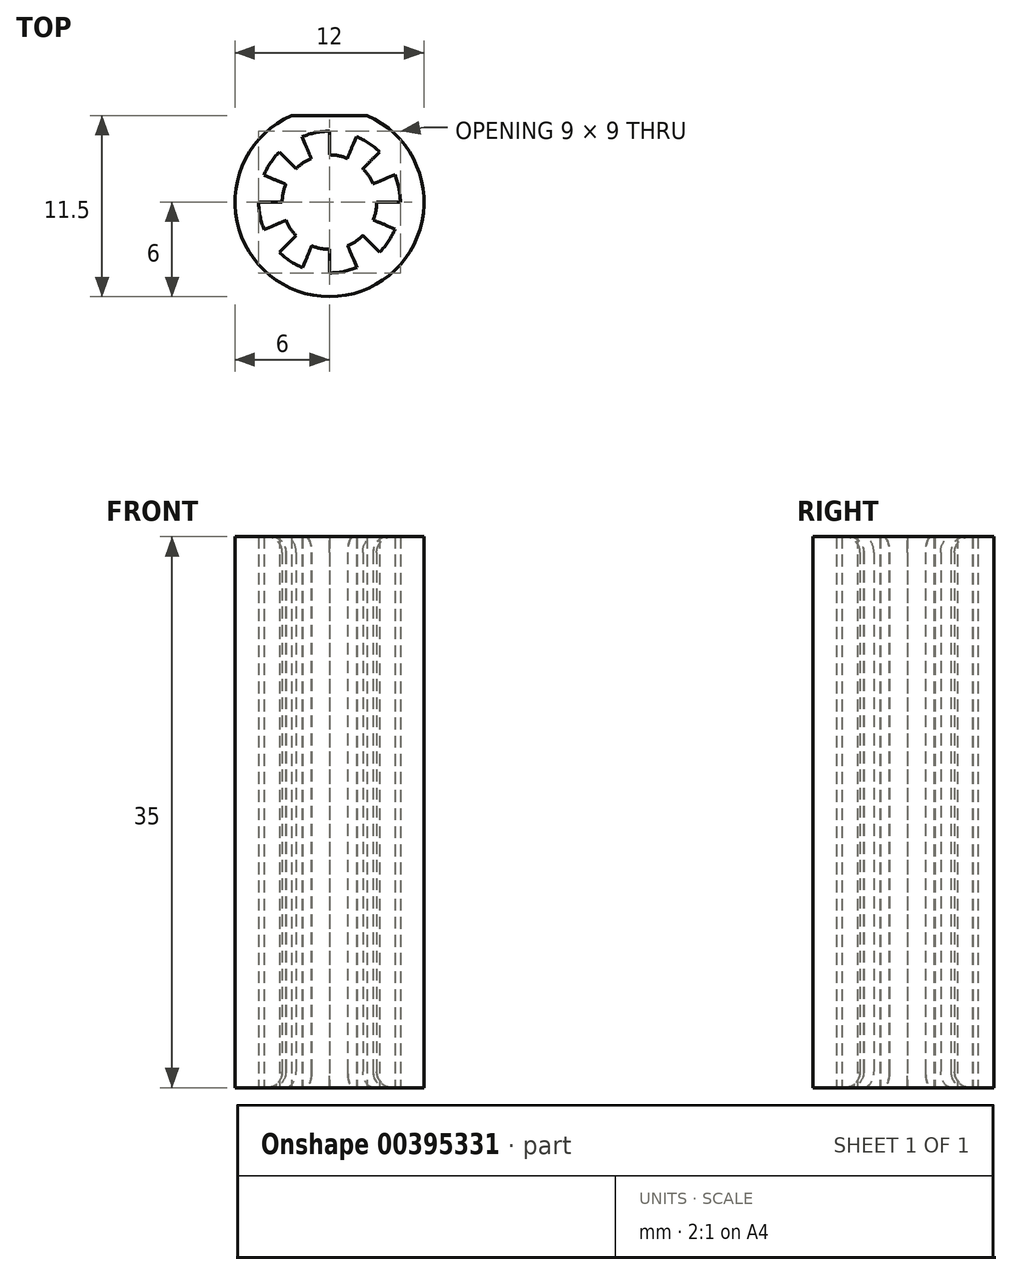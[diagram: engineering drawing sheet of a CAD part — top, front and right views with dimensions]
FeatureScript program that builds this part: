
annotation { "Feature Type Name" : "Feature", "Feature Type Description" : "" }
export const myFeature = defineFeature(function(context is Context, id is Id, definition is map)
    precondition{}
    {
        {
            var Q0;
            Q0=qCreatedBy(makeId("Top.planeOp"),FACE);
            var sketch = newSketch(context, id + "F0", { "sketchPlane" : qUnion([Q0])});
            skCircle(sketch, "E0", {"center": v(0, 0) * mm, "radius": 3 * mm});
            skCircle(sketch, "E1", {"center": v(0, 0) * mm, "radius": 6 * mm});
            skCircle(sketch, "E2", {"center": v(0, 0) * mm, "radius": 4.5 * mm});
            skLineSegment(sketch, "E3", {"start": v(0, 6) * mm, "end": v(0, -6) * mm});
            skLineSegment(sketch, "E4", {"start": v(-6, 0) * mm, "end": v(6, 0) * mm});
            skPoint(sketch, "E5", {"position": v(4.56, 3.9) * mm});
            skPoint(sketch, "E6", {"position": v(-4.24, 4.24) * mm});
            skPoint(sketch, "E7", {"position": v(-4.52, -3.95) * mm});
            skPoint(sketch, "E8", {"position": v(4.86, -3.52) * mm});
            skLineSegment(sketch, "E9", {"start": v(0, 0) * mm, "end": v(-4.24, 4.24) * mm});
            skPoint(sketch, "E10", {"position": v(-2.32, 5.53) * mm});
            skPoint(sketch, "E11", {"position": v(-5.54, 2.3) * mm});
            skLineSegment(sketch, "E12", {"start": v(-5.54, 2.3) * mm, "end": v(0, 0) * mm});
            skLineSegment(sketch, "E13", {"start": v(-2.32, 5.53) * mm, "end": v(0, 0) * mm});
            skSolve(sketch);
        }
        {
            var Q0;
            {var subQ0=sQuery(id+"F0.wireOp",EDGE,"E3");var subQ1=sQuery(id+"F0.wireOp",EDGE,"E1");var subQ2=makeQuery(id+"F0.imprint","INTERSECT",VERTEX,{"disambiguationData":[OD(0.0)],"derivedFrom":[subQ1,subQ0]});Q0=makeQuery(id+"F0.imprint","IMPRINT",FACE,{"disambiguationData":[TD([[makeQuery(id+"F0.imprint","IMPRINT",EDGE,{"disambiguationData":[TD([[subQ2,-1.0]])],"derivedFrom":subQ1}),1.0]])]});}
            var Q1;
            {var subQ0=sQuery(id+"F0.wireOp",EDGE,"E13");var subQ1=sQuery(id+"F0.wireOp",EDGE,"E0");var subQ2=makeQuery(id+"F0.imprint","INTERSECT",VERTEX,{"derivedFrom":[subQ1,subQ0]});Q1=makeQuery(id+"F0.imprint","IMPRINT",FACE,{"disambiguationData":[TD([[makeQuery(id+"F0.imprint","IMPRINT",EDGE,{"disambiguationData":[TD([[subQ2,-1.0]])],"derivedFrom":subQ1}),-1.0]])]});}
            var Q2;
            {var subQ0=sQuery(id+"F0.wireOp",EDGE,"E9");var subQ1=sQuery(id+"F0.wireOp",EDGE,"E1");var subQ2=makeQuery(id+"F0.imprint","INTERSECT",VERTEX,{"derivedFrom":[subQ1,subQ0]});Q2=makeQuery(id+"F0.imprint","IMPRINT",FACE,{"disambiguationData":[TD([[makeQuery(id+"F0.imprint","IMPRINT",EDGE,{"disambiguationData":[TD([[subQ2,1.0]])],"derivedFrom":subQ1}),1.0]])]});}
            extrude(context, id + "F1", {"entities" : qUnion([Q0, Q1, Q2]), "depth" : 35 * mm});
        }
        {
            var Q0;
            Q0=qCreatedBy(makeId("Front.planeOp"),FACE);
            var sketch = newSketch(context, id + "F2", { "sketchPlane" : qUnion([Q0])});
            skLineSegment(sketch, "E14", {"start": v(0, 46.48) * mm, "end": v(0, -20.09) * mm, "construction": true});
            skSolve(sketch);
        }
        {
            var Q0;
            Q0=makeQuery(id+"F1.opExtrude","SWEPT_BODY",BODY,{"disambiguationData":[OSD([sQuery(id+"F0.wireOp",EDGE,"E0"),sQuery(id+"F0.wireOp",EDGE,"E1"),sQuery(id+"F0.wireOp",EDGE,"E2"),sQuery(id+"F0.wireOp",EDGE,"E3"),sQuery(id+"F0.wireOp",EDGE,"E4"),sQuery(id+"F0.wireOp",EDGE,"E9")])]});
            var Q1;
            Q1=sQuery(id+"F2.wireOp",EDGE,"E14");
            circularPattern(context, id + "F3", {"entities" : qUnion([Q0]), "axis" : qUnion([Q1]), "angle" : 360 * degree, "instanceCount" : 8, "oppositeDirection" : true, "equalSpace" : true});
        }
        {
            var Q0;
            Q0=makeQuery(id+"F1.opExtrude","SWEPT_BODY",BODY,{"disambiguationData":[OSD([sQuery(id+"F0.wireOp",EDGE,"E0"),sQuery(id+"F0.wireOp",EDGE,"E1"),sQuery(id+"F0.wireOp",EDGE,"E2"),sQuery(id+"F0.wireOp",EDGE,"E3"),sQuery(id+"F0.wireOp",EDGE,"E9"),sQuery(id+"F0.wireOp",EDGE,"E13")])]});
            var Q1;
            Q1=makeQuery(id+"F3.opPattern","COPY",BODY,{"derivedFrom":makeQuery(id+"F1.opExtrude","SWEPT_BODY",BODY,{"disambiguationData":[OSD([sQuery(id+"F0.wireOp",EDGE,"E0"),sQuery(id+"F0.wireOp",EDGE,"E1"),sQuery(id+"F0.wireOp",EDGE,"E2"),sQuery(id+"F0.wireOp",EDGE,"E3"),sQuery(id+"F0.wireOp",EDGE,"E9"),sQuery(id+"F0.wireOp",EDGE,"E13")])]}),"instanceName":"1"});
            var Q2;
            Q2=makeQuery(id+"F3.opPattern","COPY",BODY,{"derivedFrom":makeQuery(id+"F1.opExtrude","SWEPT_BODY",BODY,{"disambiguationData":[OSD([sQuery(id+"F0.wireOp",EDGE,"E0"),sQuery(id+"F0.wireOp",EDGE,"E1"),sQuery(id+"F0.wireOp",EDGE,"E2"),sQuery(id+"F0.wireOp",EDGE,"E3"),sQuery(id+"F0.wireOp",EDGE,"E9"),sQuery(id+"F0.wireOp",EDGE,"E13")])]}),"instanceName":"2"});
            var Q3;
            Q3=makeQuery(id+"F3.opPattern","COPY",BODY,{"derivedFrom":makeQuery(id+"F1.opExtrude","SWEPT_BODY",BODY,{"disambiguationData":[OSD([sQuery(id+"F0.wireOp",EDGE,"E0"),sQuery(id+"F0.wireOp",EDGE,"E1"),sQuery(id+"F0.wireOp",EDGE,"E2"),sQuery(id+"F0.wireOp",EDGE,"E3"),sQuery(id+"F0.wireOp",EDGE,"E9"),sQuery(id+"F0.wireOp",EDGE,"E13")])]}),"instanceName":"3"});
            var Q4;
            Q4=makeQuery(id+"F3.opPattern","COPY",BODY,{"derivedFrom":makeQuery(id+"F1.opExtrude","SWEPT_BODY",BODY,{"disambiguationData":[OSD([sQuery(id+"F0.wireOp",EDGE,"E0"),sQuery(id+"F0.wireOp",EDGE,"E1"),sQuery(id+"F0.wireOp",EDGE,"E2"),sQuery(id+"F0.wireOp",EDGE,"E3"),sQuery(id+"F0.wireOp",EDGE,"E9"),sQuery(id+"F0.wireOp",EDGE,"E13")])]}),"instanceName":"4"});
            var Q5;
            Q5=makeQuery(id+"F3.opPattern","COPY",BODY,{"derivedFrom":makeQuery(id+"F1.opExtrude","SWEPT_BODY",BODY,{"disambiguationData":[OSD([sQuery(id+"F0.wireOp",EDGE,"E0"),sQuery(id+"F0.wireOp",EDGE,"E1"),sQuery(id+"F0.wireOp",EDGE,"E2"),sQuery(id+"F0.wireOp",EDGE,"E3"),sQuery(id+"F0.wireOp",EDGE,"E9"),sQuery(id+"F0.wireOp",EDGE,"E13")])]}),"instanceName":"5"});
            var Q6;
            Q6=makeQuery(id+"F3.opPattern","COPY",BODY,{"derivedFrom":makeQuery(id+"F1.opExtrude","SWEPT_BODY",BODY,{"disambiguationData":[OSD([sQuery(id+"F0.wireOp",EDGE,"E0"),sQuery(id+"F0.wireOp",EDGE,"E1"),sQuery(id+"F0.wireOp",EDGE,"E2"),sQuery(id+"F0.wireOp",EDGE,"E3"),sQuery(id+"F0.wireOp",EDGE,"E9"),sQuery(id+"F0.wireOp",EDGE,"E13")])]}),"instanceName":"6"});
            var Q7;
            Q7=makeQuery(id+"F3.opPattern","COPY",BODY,{"derivedFrom":makeQuery(id+"F1.opExtrude","SWEPT_BODY",BODY,{"disambiguationData":[OSD([sQuery(id+"F0.wireOp",EDGE,"E0"),sQuery(id+"F0.wireOp",EDGE,"E1"),sQuery(id+"F0.wireOp",EDGE,"E2"),sQuery(id+"F0.wireOp",EDGE,"E3"),sQuery(id+"F0.wireOp",EDGE,"E9"),sQuery(id+"F0.wireOp",EDGE,"E13")])]}),"instanceName":"7"});
            booleanBodies(context, id + "F4", {"operationType" : BooleanOperationType.UNION, "tools" : qUnion([Q0, Q1, Q2, Q3, Q4, Q5, Q6, Q7])});
        }
        {
            var Q0;
            Q0=makeQuery(id+"F3.opPattern","COPY",EDGE,{"derivedFrom":makeQuery(id+"F1.opExtrude","CAP_EDGE",EDGE,{"disambiguationData":[OSD([sQuery(id+"F0.wireOp",EDGE,"E0")])],"isStart":false}),"instanceName":"1"});
            var Q1;
            Q1=makeQuery(id+"F1.opExtrude","CAP_EDGE",EDGE,{"disambiguationData":[OSD([sQuery(id+"F0.wireOp",EDGE,"E0")])],"isStart":false});
            var Q2;
            Q2=makeQuery(id+"F3.opPattern","COPY",EDGE,{"derivedFrom":makeQuery(id+"F1.opExtrude","CAP_EDGE",EDGE,{"disambiguationData":[OSD([sQuery(id+"F0.wireOp",EDGE,"E0")])],"isStart":false}),"instanceName":"7"});
            var Q3;
            Q3=makeQuery(id+"F3.opPattern","COPY",EDGE,{"derivedFrom":makeQuery(id+"F1.opExtrude","CAP_EDGE",EDGE,{"disambiguationData":[OSD([sQuery(id+"F0.wireOp",EDGE,"E0")])],"isStart":false}),"instanceName":"6"});
            var Q4;
            Q4=makeQuery(id+"F3.opPattern","COPY",EDGE,{"derivedFrom":makeQuery(id+"F1.opExtrude","CAP_EDGE",EDGE,{"disambiguationData":[OSD([sQuery(id+"F0.wireOp",EDGE,"E0")])],"isStart":false}),"instanceName":"5"});
            var Q5;
            Q5=makeQuery(id+"F3.opPattern","COPY",EDGE,{"derivedFrom":makeQuery(id+"F1.opExtrude","CAP_EDGE",EDGE,{"disambiguationData":[OSD([sQuery(id+"F0.wireOp",EDGE,"E0")])],"isStart":false}),"instanceName":"4"});
            var Q6;
            Q6=makeQuery(id+"F3.opPattern","COPY",EDGE,{"derivedFrom":makeQuery(id+"F1.opExtrude","CAP_EDGE",EDGE,{"disambiguationData":[OSD([sQuery(id+"F0.wireOp",EDGE,"E0")])],"isStart":false}),"instanceName":"3"});
            var Q7;
            Q7=makeQuery(id+"F3.opPattern","COPY",EDGE,{"derivedFrom":makeQuery(id+"F1.opExtrude","CAP_EDGE",EDGE,{"disambiguationData":[OSD([sQuery(id+"F0.wireOp",EDGE,"E0")])],"isStart":false}),"instanceName":"2"});
            var Q8;
            Q8=makeQuery(id+"F3.opPattern","COPY",EDGE,{"derivedFrom":makeQuery(id+"F1.opExtrude","CAP_EDGE",EDGE,{"disambiguationData":[OSD([sQuery(id+"F0.wireOp",EDGE,"E0")])],"isStart":true}),"instanceName":"5"});
            var Q9;
            Q9=makeQuery(id+"F3.opPattern","COPY",EDGE,{"derivedFrom":makeQuery(id+"F1.opExtrude","CAP_EDGE",EDGE,{"disambiguationData":[OSD([sQuery(id+"F0.wireOp",EDGE,"E0")])],"isStart":true}),"instanceName":"6"});
            var Q10;
            Q10=makeQuery(id+"F3.opPattern","COPY",EDGE,{"derivedFrom":makeQuery(id+"F1.opExtrude","CAP_EDGE",EDGE,{"disambiguationData":[OSD([sQuery(id+"F0.wireOp",EDGE,"E0")])],"isStart":true}),"instanceName":"7"});
            var Q11;
            Q11=makeQuery(id+"F1.opExtrude","CAP_EDGE",EDGE,{"disambiguationData":[OSD([sQuery(id+"F0.wireOp",EDGE,"E0")])],"isStart":true});
            var Q12;
            Q12=makeQuery(id+"F3.opPattern","COPY",EDGE,{"derivedFrom":makeQuery(id+"F1.opExtrude","CAP_EDGE",EDGE,{"disambiguationData":[OSD([sQuery(id+"F0.wireOp",EDGE,"E0")])],"isStart":true}),"instanceName":"1"});
            var Q13;
            Q13=makeQuery(id+"F3.opPattern","COPY",EDGE,{"derivedFrom":makeQuery(id+"F1.opExtrude","CAP_EDGE",EDGE,{"disambiguationData":[OSD([sQuery(id+"F0.wireOp",EDGE,"E0")])],"isStart":true}),"instanceName":"2"});
            var Q14;
            Q14=makeQuery(id+"F3.opPattern","COPY",EDGE,{"derivedFrom":makeQuery(id+"F1.opExtrude","CAP_EDGE",EDGE,{"disambiguationData":[OSD([sQuery(id+"F0.wireOp",EDGE,"E0")])],"isStart":true}),"instanceName":"3"});
            var Q15;
            Q15=makeQuery(id+"F3.opPattern","COPY",EDGE,{"derivedFrom":makeQuery(id+"F1.opExtrude","CAP_EDGE",EDGE,{"disambiguationData":[OSD([sQuery(id+"F0.wireOp",EDGE,"E0")])],"isStart":true}),"instanceName":"4"});
            fillet(context, id + "F5", {"entities" : qUnion([Q0, Q1, Q2, Q3, Q4, Q5, Q6, Q7, Q8, Q9, Q10, Q11, Q12, Q13, Q14, Q15]), "radius" : 1 * mm, "tangentPropagation" : true, "allowEdgeOverflow" : false});
        }
        {
            var Q0;
            {var subQ0=makeQuery(id+"F1.opExtrude","CAP_FACE",FACE,{"disambiguationData":[OSD([sQuery(id+"F0.wireOp",EDGE,"E0"),sQuery(id+"F0.wireOp",EDGE,"E1"),sQuery(id+"F0.wireOp",EDGE,"E2"),sQuery(id+"F0.wireOp",EDGE,"E3"),sQuery(id+"F0.wireOp",EDGE,"E9"),sQuery(id+"F0.wireOp",EDGE,"E13")])],"isStart":false});Q0=makeQuery(id+"F4.opBoolean","MERGE",FACE,{"derivedFrom":[subQ0,makeQuery(id+"F3.opPattern","COPY",FACE,{"derivedFrom":subQ0,"instanceName":"1"}),makeQuery(id+"F3.opPattern","COPY",FACE,{"derivedFrom":subQ0,"instanceName":"2"}),makeQuery(id+"F3.opPattern","COPY",FACE,{"derivedFrom":subQ0,"instanceName":"3"}),makeQuery(id+"F3.opPattern","COPY",FACE,{"derivedFrom":subQ0,"instanceName":"4"}),makeQuery(id+"F3.opPattern","COPY",FACE,{"derivedFrom":subQ0,"instanceName":"5"}),makeQuery(id+"F3.opPattern","COPY",FACE,{"derivedFrom":subQ0,"instanceName":"6"}),makeQuery(id+"F3.opPattern","COPY",FACE,{"derivedFrom":subQ0,"instanceName":"7"})]});}
            var sketch = newSketch(context, id + "F6", { "sketchPlane" : qUnion([Q0])});
            skPoint(sketch, "E15", {"position": v(0, 6) * mm});
            skLineSegment(sketch, "E16.bottom", {"start": v(-3.87, 5.5) * mm, "end": v(3.87, 5.5) * mm});
            skLineSegment(sketch, "E16.top", {"start": v(-3.87, 6.5) * mm, "end": v(3.87, 6.5) * mm});
            skLineSegment(sketch, "E16.left", {"start": v(-3.87, 5.5) * mm, "end": v(-3.87, 6.5) * mm});
            skLineSegment(sketch, "E16.right", {"start": v(3.87, 5.5) * mm, "end": v(3.87, 6.5) * mm});
            skSolve(sketch);
        }
        {
            var Q0;
            Q0 = qSketchRegion(id + "F6", true);
            extrude(context, id + "F7", {"entities" : qUnion([Q0]), "operationType" : NewBodyOperationType.REMOVE, "oppositeDirection" : true, "depth" : 35 * mm});
        }
    });
